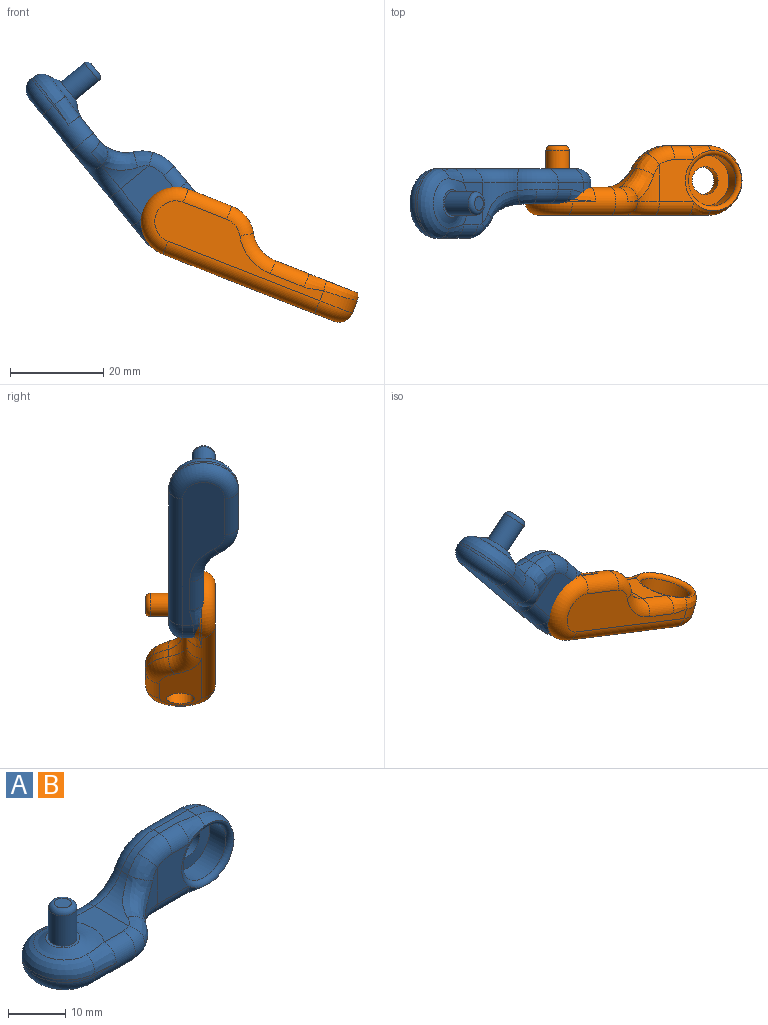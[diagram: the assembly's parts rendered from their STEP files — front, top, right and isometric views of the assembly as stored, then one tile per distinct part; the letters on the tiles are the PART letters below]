
ASSEMBLY  parts=2 mates=1
PART A: 43 faces, bbox 57.1x26.6x16.4 mm
  f0: plane 5.29x0.4mm, normal (0,1,0), area 1mm2, adj f13,f25,f26
  f1: plane 8.5x2.24mm, normal (0,0,1), area 14.1mm2, adj f14,f15,f22,f37,f39
  f2: plane 5.29x0.4mm, normal (0,-1,0), area 1mm2, adj f13,f30,f31
  f3: plane 27.7x9mm, normal (0,1,0), area 138.4mm2, adj f21,f22,f23,f24,f25,f42
  f4: plane 39.5x9mm, normal (0,0,-1), area 201.2mm2, adj f14,f25,f27,f29,f30,f32,f33,f34
  f5: plane 9x6.52mm, normal (0,0,1), area 49mm2, adj f16,f19,f25,f30,f33
  f6: plane 9x7.82mm, normal (0,-1,0), area 57.9mm2, adj f18,f20,f32,f39,f41
  f7: plane 6x6mm, normal (0,0,1), area 8.6mm2, adj f8,f16
  f8: cylinder r=2.5mm len=6.5mm, axis (0,0,-1), area 102.1mm2, adj f7,f17
  f9: plane 3x3mm, normal (0,0,1), area 7.1mm2, adj f17
  f10: cylinder r=5.5mm len=11mm, axis (0,-1,0), area 138.2mm2, adj f11,f18
  f11: plane 11x11mm, normal (0,-1,0), area 66.8mm2, adj f10,f42
  f12: cylinder r=7.5mm len=3.49mm, axis (0,0,-1), area 0.5mm2, adj f20,f33,f36
  f13: cylinder r=7.5mm len=15mm, axis (0,0,1), area 9.4mm2, adj f0,f2,f27,f28
  f14: cylinder r=7.5mm len=15mm, axis (0,-1,0), area 52.8mm2, adj f1,f4,f24,f35
  f15: cylinder r=9mm len=8.02mm, axis (0,-1,0), area 15.2mm2, adj f1,f19,f21,f40,f41
  f16: torus R=7.33mm, axis (0,0,1), area 91.7mm2, adj f5,f7,f26,f28,f31
  f17: torus R=1.5mm, axis (0,0,1), area 21.1mm2, adj f8,f9
  f18: torus R=6.5mm, axis (0,-1,0), area 57.9mm2, adj f6,f10,f34,f35,f37
  f19: cylinder r=7.5mm len=8.62mm, axis (0,-1,0), area 32.8mm2, adj f5,f15,f23,f36,f38
  f20: cylinder r=7.5mm len=7.87mm, axis (0,0,-1), area 21.3mm2, adj f6,f12,f29,f38,f40
  f21: torus R=6mm, axis (0,1,0), area 41mm2, adj f3,f15,f22,f23
  f22: cylinder r=3mm len=8.5mm, axis (1,0,0), area 40.1mm2, adj f1,f3,f21,f24
  f23: torus R=10.5mm, axis (0,1,0), area 44.5mm2, adj f3,f19,f21,f25
  f24: torus R=4.5mm, axis (0,1,0), area 94.9mm2, adj f3,f14,f22,f25
  f25: cylinder r=3mm len=35mm, axis (1,0,0), area 195.6mm2, adj f0,f3,f4,f5,f23,f24,f26,f27
  f26: bspline ~8.58x3.45mm, area 22.2mm2, adj f0,f16,f25,f28
  f27: torus R=4.5mm, axis (0,0,1), area 94.9mm2, adj f4,f13,f25,f30
  f28: bspline ~15.01x9.25mm, area 80.4mm2, adj f13,f16,f26,f31
  f29: torus R=10.5mm, axis (0,0,1), area 42.4mm2, adj f4,f20,f32,f33
  f30: cylinder r=3mm len=10mm, axis (1,0,0), area 69.3mm2, adj f2,f4,f5,f27,f31,f33
  f31: bspline ~8.58x3.45mm, area 22.2mm2, adj f2,f16,f28,f30
  f32: cylinder r=3mm len=7.82mm, axis (-1,0,0), area 36.8mm2, adj f4,f6,f29,f34
  f33: torus R=4.5mm, axis (0,0,1), area 44.1mm2, adj f4,f5,f12,f29,f30,f36
  f34: bspline ~5.11x3.2mm, area 13.9mm2, adj f4,f18,f32,f35
  f35: bspline ~15x7.71mm, area 47.8mm2, adj f14,f18,f34,f37
  f36: bspline ~6.01x6.01mm, area 18.9mm2, adj f12,f19,f33,f38
  f37: bspline ~5.11x3.2mm, area 13.9mm2, adj f1,f18,f35,f39
  f38: bspline ~9.1x7.88mm, area 43.3mm2, adj f19,f20,f36,f40
  f39: cylinder r=3mm len=4.31mm, axis (1,0,0), area 20.3mm2, adj f1,f6,f37,f41
  f40: bspline ~6.73x5.97mm, area 17.6mm2, adj f15,f20,f38,f41
  f41: torus R=6mm, axis (0,-1,0), area 23.3mm2, adj f6,f15,f39,f40
  f42: cylinder r=3mm len=6mm, axis (0,-1,0), area 47.1mm2, adj f3,f11
PART B: same geometry as A
PLACE A rot(axis=(0,1,0),50.9deg) t=(-13.93,66.09,11.86)mm fixed
PLACE B rot(axis=(-0.97,0.18,0.18),92deg) t=(17.23,61.58,-8.61)mm
MATE revolute B.f8 <-> A.f10  axis (0,-1,0) through (7.53,69.08,-2.65)mm
